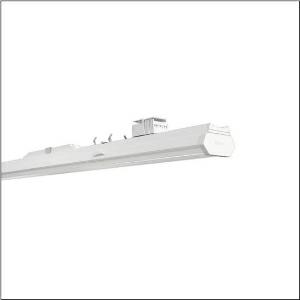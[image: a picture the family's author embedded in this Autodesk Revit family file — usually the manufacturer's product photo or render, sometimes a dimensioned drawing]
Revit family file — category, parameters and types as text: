
# Revit family: licross_r__11_protected_mo_51td1bdn69xg_78b7
name_source: partatom
category: Lighting Fixtures
units: mm (PartAtom-declared; Revit-internal decimal feet)

## family parameters
Cut with Voids When Loaded = No
Host = Face
Light Source = No
Part Type = Normal
Room Calculation Point = No
Round Connector Dimension = Use Diameter
Shared = No

## types (1)
- --- (1 x LED, 9140 lm, 57.1 W, 6500K)
    Apparent Load = 57 VA
    CIE Flux Codes = 54 82 95 97 100
    Color Rendering = 80
    Color Temperature = 6500K
    Default Elevation = 1800 mm
    Description = Licross® 11 Protected MO, luminaire insert, of sheet steel, galvanised, coil coated, white, length: 1.500mm, width: 90mm, height: 101mm, LED rated luminous flux: 9.140lm, light colour: 865, control gear: DALI 2, with plug, 5-pole, with phase selection, mains connection: 220..240V, AC, 50/60Hz, rated input power: 57W, internal wiring halogen-free, primary optical cover: cover, of PMMA, light emission: direct distribution, primary light characteristic: symmetric, protection rating (complete): IP54, insulation class (complete): insulation class I (protective earthing), certification: CE, ENEC, VDE, UKCA, protection symbol: D if used in an environment with non-conductive dust loads with corresponding accessories, impact resistance: IK06, permissible ambient temperature for indoor applications: -25..+35°C, corresponds to IFS (International Featured Standards) requirements for safety and quality in the food industry, reducing of maximum allowable ambient temperature of 5°C with ceiling mounting, LABS conformity tested according to VDMA 24364:2018-05, packaging unit: 1 piece
    Height = 92 mm
    Lamp = 1 x LED
    Lamp Light Flux = 9140 lm
    Lamp Power = 57.1 W
    Lamp count = 1
    Length = 1500 mm
    Luminous efficacy = 160 lm/W
    Manufacturer = Siteco
    ModVariant = No
    Model = 51TD1BDN69XG
    Mounting Place = Ceiling
    Mounting Type = Pendant
    Number of Poles = 1
    OnlyDefault = Yes
    Power Factor = 1
    Product Name = Licross® 11 Protected MO
    Product group = luminaire insert | ceiling pendant
    ProductGroupID = 902
    Protection Class = Protection class I
    Protection Degree = IP 54
    RLX_Detail_Level = 1
    RLX_Emergency_Light_Flux = 0 lm
    RLX_Emergency_Type = 0
    RLX_Emergency_Type_DB = No
    RlxData = <blob elided: 24249 chars, md5=6cf304c7>
    Socket = socket
    Standby Power = 0 W
    System Light Flux = 9140 lm
    System Power = 57 W
    Type Comments = factory setting: luminous flux: 100 % | dim-lin: 254 | 378 mA
    Type Image = l_1256145.jpg
    URL = http://relux.com
    VarID = @adj_089419
    Voltage = 0 V
    Weight = 0.00 kg
    Width = 88 mm

## geometry (parser evidence)
native form markers: Blend x4, Sweep x11
no freeform markers — native parametric forms only
